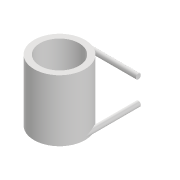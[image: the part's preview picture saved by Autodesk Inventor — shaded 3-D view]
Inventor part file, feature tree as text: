
AUTODESK INVENTOR PART (.ipt)
format: ipt  version: 2022 (Build 260153000, 153)  size: 117,760 bytes
history: native  units: mm
features: extrude x3, sketch x3, projected_geometry x2
ambient origin geometry x8: Origin, YZ Plane, XZ Plane, XY Plane, X Axis, Y Axis, Z Axis, Center Point
bodies: Solid1 (feature_tree)
feature tree (8):
  extrude  "Extrusion1"  Depth=7.0mm
  extrude  "Extrusion2"  Depth=10.0mm TaperAngle=0.0deg
  extrude  "Extrusion3"  Depth=10.0mm
  sketch  "Sketch1"  dims[d0=9.1mm d1=7.0mm]
  sketch  "Sketch2"  dims[d2=11.0mm d3=0.0mm d5=10.0mm d6=0.0mm]
  projected_geometry  "Projected Loop1"
  sketch  "Sketch3"  dims[d8=10.0mm d9=0.0mm d11=0.9mm d12=0.9mm]
  projected_geometry  "Projected Loop2"
